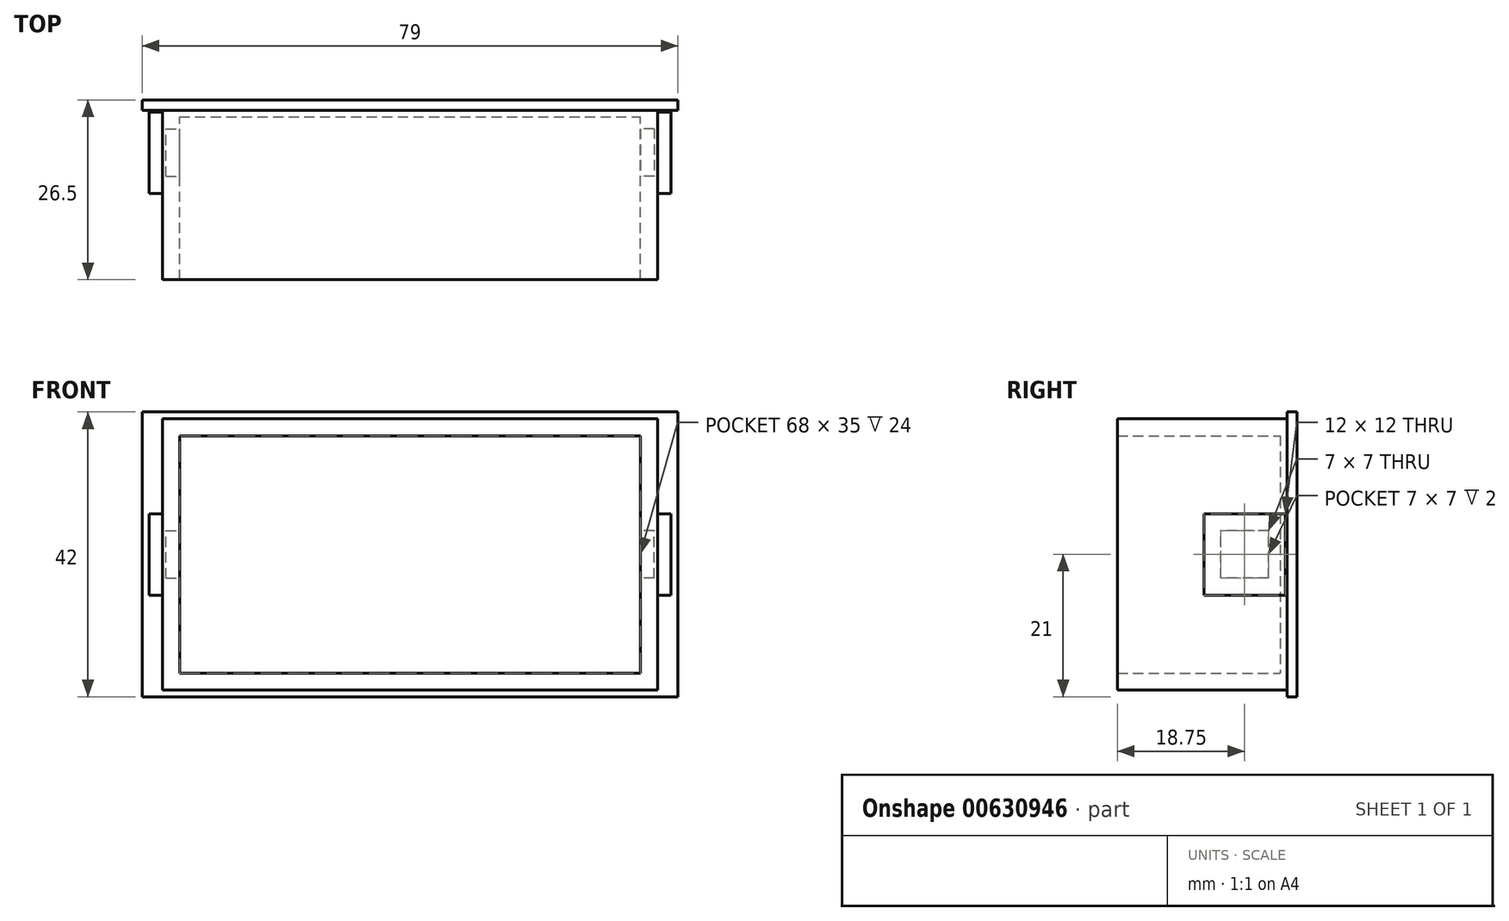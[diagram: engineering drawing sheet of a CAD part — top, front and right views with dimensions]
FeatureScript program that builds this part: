
annotation { "Feature Type Name" : "Feature", "Feature Type Description" : "" }
export const myFeature = defineFeature(function(context is Context, id is Id, definition is map)
    precondition{}
    {
        {
            var Q0;
            Q0=qCreatedBy(makeId("Front.planeOp"),FACE);
            var sketch = newSketch(context, id + "F0", { "sketchPlane" : qUnion([Q0])});
            skLineSegment(sketch, "E0.bottom", {"start": v(39.5, -21) * mm, "end": v(-39.5, -21) * mm});
            skLineSegment(sketch, "E0.top", {"start": v(39.5, 21) * mm, "end": v(-39.5, 21) * mm});
            skLineSegment(sketch, "E0.left", {"start": v(39.5, -21) * mm, "end": v(39.5, 21) * mm});
            skLineSegment(sketch, "E0.right", {"start": v(-39.5, -21) * mm, "end": v(-39.5, 21) * mm});
            skPoint(sketch, "E0.middle", {"position": v(0, 0) * mm});
            skLineSegment(sketch, "E1.bottom", {"start": v(36.5, -20) * mm, "end": v(-36.5, -20) * mm});
            skLineSegment(sketch, "E1.top", {"start": v(36.5, 20) * mm, "end": v(-36.5, 20) * mm});
            skLineSegment(sketch, "E1.left", {"start": v(36.5, -20) * mm, "end": v(36.5, 20) * mm});
            skLineSegment(sketch, "E1.right", {"start": v(-36.5, -20) * mm, "end": v(-36.5, 20) * mm});
            skSolve(sketch);
        }
        {
            var Q0;
            Q0=makeQuery(id+"F0.imprint","IMPRINT",FACE,{"disambiguationData":[TD([[makeQuery(id+"F0.imprint","IMPRINT",EDGE,{"derivedFrom":sQuery(id+"F0.wireOp",EDGE,"E1.bottom")}),-1.0]])]});
            extrude(context, id + "F1", {"entities" : qUnion([Q0]), "depth" : 26.5 * mm, "offsetDistance" : 25.4 * mm});
        }
        {
            var Q0;
            Q0=makeQuery(id+"F0.imprint","IMPRINT",FACE,{"disambiguationData":[TD([[makeQuery(id+"F0.imprint","IMPRINT",EDGE,{"derivedFrom":sQuery(id+"F0.wireOp",EDGE,"E0.bottom")}),-1.0]])]});
            extrude(context, id + "F2", {"entities" : qUnion([Q0]), "operationType" : NewBodyOperationType.ADD, "depth" : 1.5 * mm, "offsetDistance" : 25 * mm});
        }
        {
            var Q0;
            Q0=makeQuery(id+"F1.opExtrude","SWEPT_FACE",FACE,{"disambiguationData":[OSD([sQuery(id+"F0.wireOp",EDGE,"E1.right")])]});
            var sketch = newSketch(context, id + "F3", { "sketchPlane" : qUnion([Q0])});
            skLineSegment(sketch, "E2.bottom", {"start": v(13.75, -6) * mm, "end": v(1.75, -6) * mm});
            skLineSegment(sketch, "E2.top", {"start": v(13.75, 6) * mm, "end": v(1.75, 6) * mm});
            skLineSegment(sketch, "E2.left", {"start": v(13.75, -6) * mm, "end": v(13.75, 6) * mm});
            skLineSegment(sketch, "E2.right", {"start": v(1.75, -6) * mm, "end": v(1.75, 6) * mm});
            skPoint(sketch, "E2.middle", {"position": v(7.75, 0) * mm});
            skPoint(sketch, "E2.middle.positionSnap0", {"position": v(1.5, 0) * mm});
            skPoint(sketch, "E2.centerSnap0", {"position": v(1.5, 0) * mm});
            skSolve(sketch);
        }
        {
            var Q0;
            Q0=makeQuery(id+"F3.imprint","IMPRINT",FACE,{"disambiguationData":[TD([[makeQuery(id+"F3.imprint","IMPRINT",EDGE,{"derivedFrom":sQuery(id+"F3.wireOp",EDGE,"E2.bottom")}),-1.0]])]});
            extrude(context, id + "F4", {"entities" : qUnion([Q0]), "operationType" : NewBodyOperationType.ADD, "depth" : 2 * mm, "offsetDistance" : 25 * mm});
        }
        {
            var Q0;
            Q0=makeQuery(id+"F1.opExtrude","SWEPT_FACE",FACE,{"disambiguationData":[OSD([sQuery(id+"F0.wireOp",EDGE,"E1.left")])]});
            var sketch = newSketch(context, id + "F5", { "sketchPlane" : qUnion([Q0])});
            skLineSegment(sketch, "E3.bottom", {"start": v(-1.75, -6) * mm, "end": v(-13.75, -6) * mm});
            skLineSegment(sketch, "E3.top", {"start": v(-1.75, 6) * mm, "end": v(-13.75, 6) * mm});
            skLineSegment(sketch, "E3.left", {"start": v(-1.75, -6) * mm, "end": v(-1.75, 6) * mm});
            skLineSegment(sketch, "E3.right", {"start": v(-13.75, -6) * mm, "end": v(-13.75, 6) * mm});
            skPoint(sketch, "E3.middle", {"position": v(-7.75, 0) * mm});
            skSolve(sketch);
        }
        {
            var Q0;
            Q0=makeQuery(id+"F5.imprint","IMPRINT",FACE,{"disambiguationData":[TD([[makeQuery(id+"F5.imprint","IMPRINT",EDGE,{"derivedFrom":sQuery(id+"F5.wireOp",EDGE,"E3.bottom")}),-1.0]])]});
            extrude(context, id + "F6", {"entities" : qUnion([Q0]), "operationType" : NewBodyOperationType.ADD, "depth" : 2 * mm, "offsetDistance" : 25 * mm});
        }
        {
            var Q0;
            Q0=makeQuery(id+"F1.opExtrude","CAP_FACE",FACE,{"disambiguationData":[OSD([sQuery(id+"F0.wireOp",EDGE,"E1.bottom"),sQuery(id+"F0.wireOp",EDGE,"E1.top"),sQuery(id+"F0.wireOp",EDGE,"E1.left"),sQuery(id+"F0.wireOp",EDGE,"E1.right")])],"isStart":false});
            shell(context, id + "F7", {"entities" : qUnion([Q0]), "thickness" : 2.5 * mm});
        }
    });
